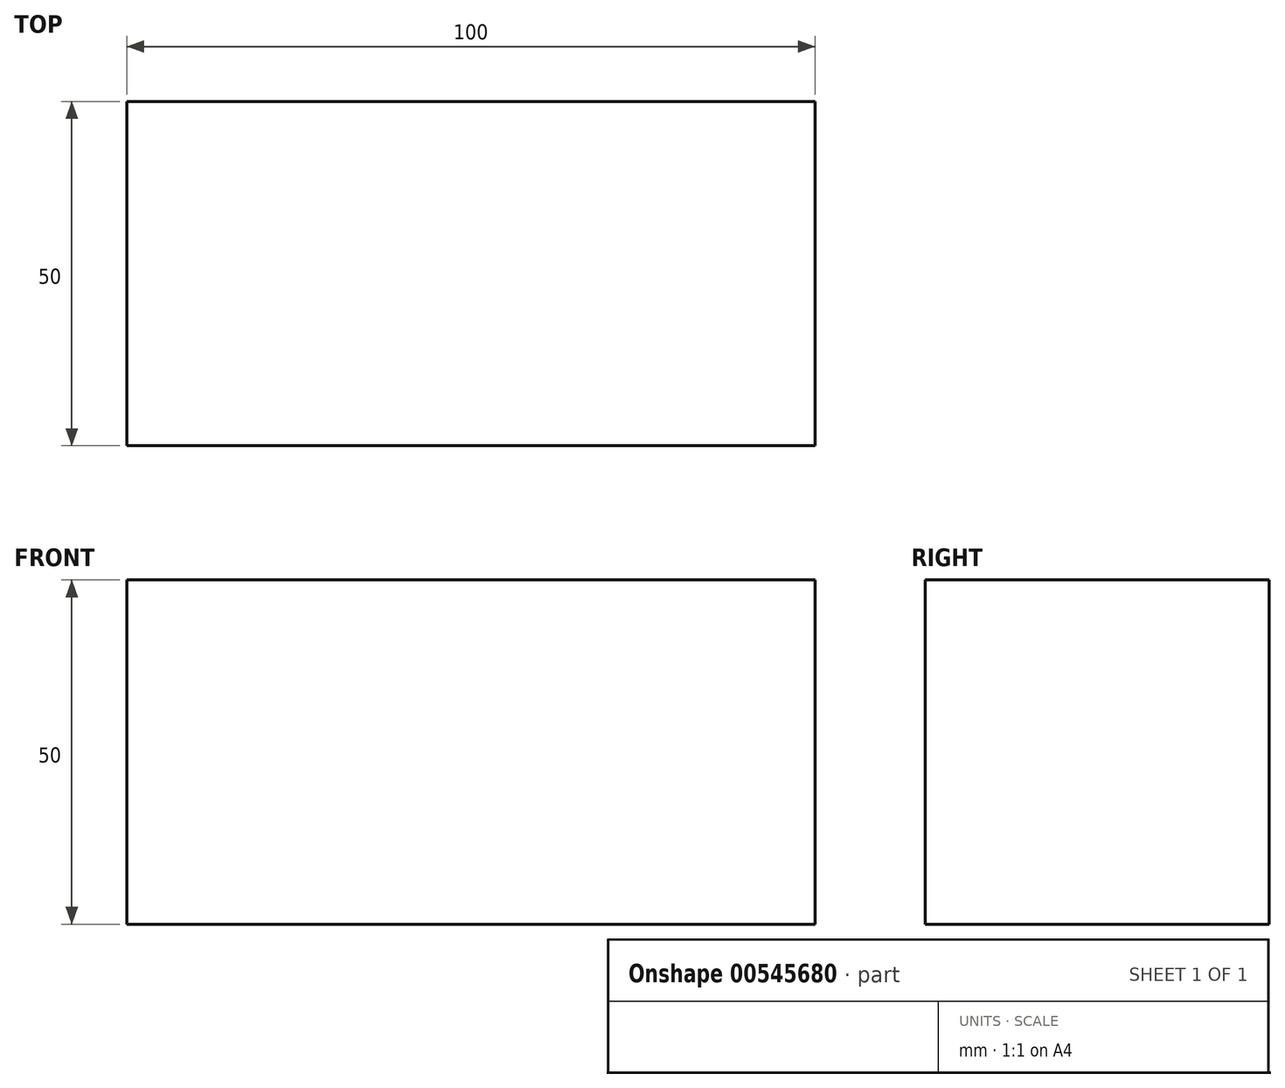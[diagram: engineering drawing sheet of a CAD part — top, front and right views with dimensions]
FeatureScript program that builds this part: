
annotation { "Feature Type Name" : "Feature", "Feature Type Description" : "" }
export const myFeature = defineFeature(function(context is Context, id is Id, definition is map)
    precondition{}
    {
        {
            var Q0;
            Q0=qCreatedBy(makeId("Top.planeOp"),FACE);
            var sketch = newSketch(context, id + "F0", { "sketchPlane" : qUnion([Q0])});
            skLineSegment(sketch, "E0.bottom", {"start": v(-40.23, 13.88) * mm, "end": v(59.77, 13.88) * mm});
            skLineSegment(sketch, "E0.top", {"start": v(-40.23, -36.12) * mm, "end": v(59.77, -36.12) * mm});
            skLineSegment(sketch, "E0.left", {"start": v(-40.23, 13.88) * mm, "end": v(-40.23, -36.12) * mm});
            skLineSegment(sketch, "E0.right", {"start": v(59.77, 13.88) * mm, "end": v(59.77, -36.12) * mm});
            skSolve(sketch);
        }
        {
            var Q0;
            Q0=makeQuery(id+"F0.imprint","IMPRINT",FACE,{"disambiguationData":[TD([[makeQuery(id+"F0.imprint","IMPRINT",EDGE,{"derivedFrom":sQuery(id+"F0.wireOp",EDGE,"E0.bottom")}),-1.0]])]});
            extrude(context, id + "F1", {"entities" : qUnion([Q0]), "depth" : 50 * mm, "offsetDistance" : 25 * mm});
        }
    });
